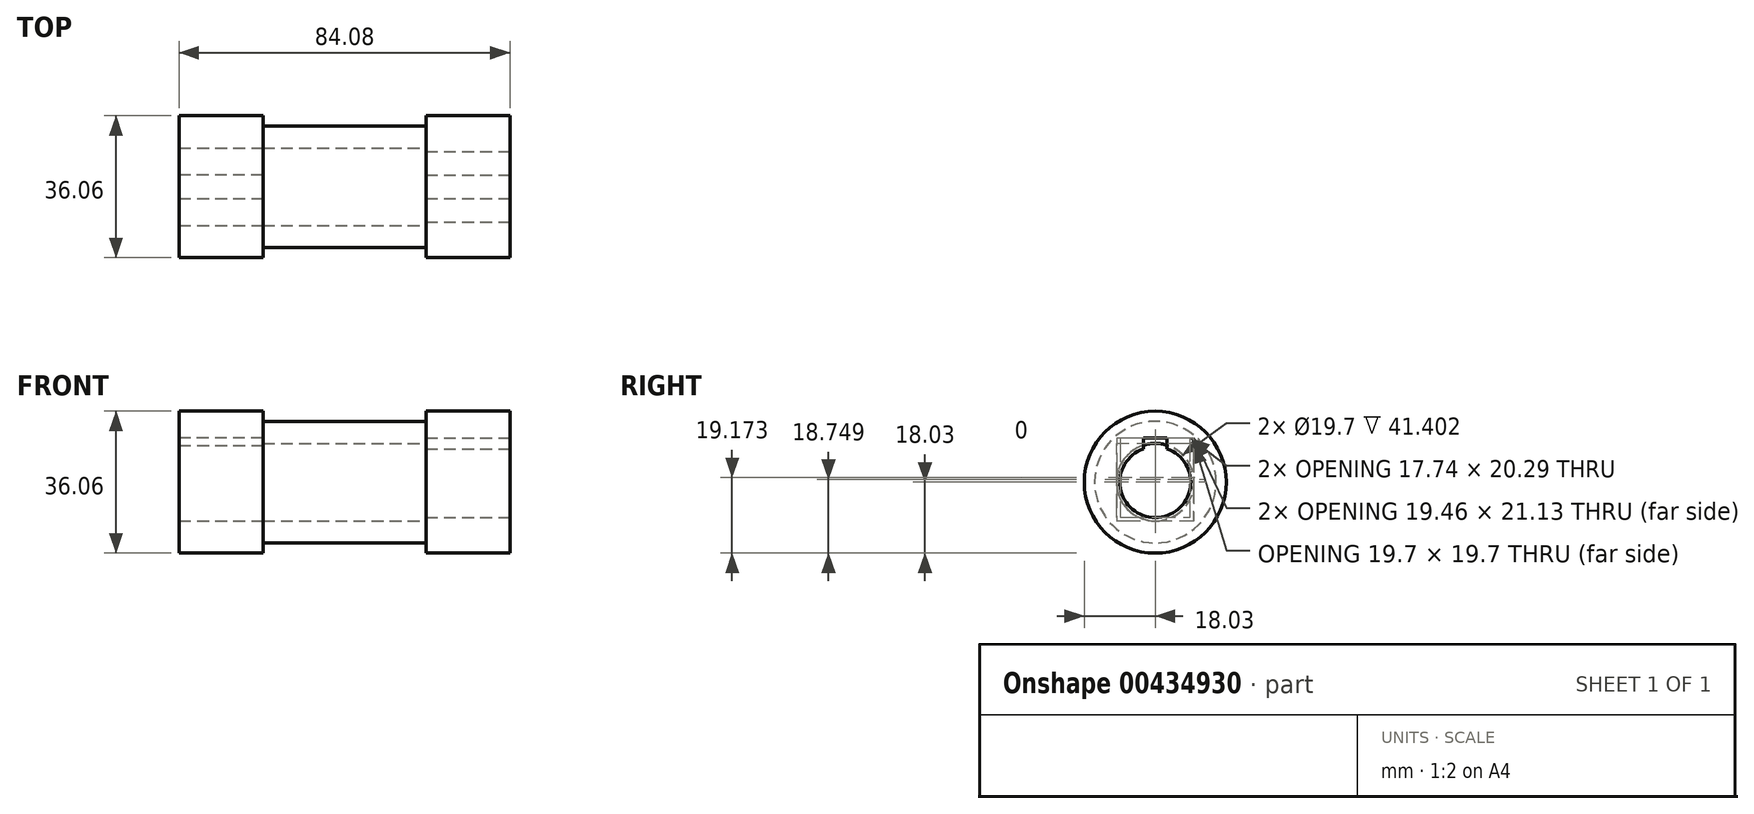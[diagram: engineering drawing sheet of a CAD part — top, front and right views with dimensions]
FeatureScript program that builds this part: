
annotation { "Feature Type Name" : "Feature", "Feature Type Description" : "" }
export const myFeature = defineFeature(function(context is Context, id is Id, definition is map)
    precondition{}
    {
        {
            var Q0;
            Q0=qCreatedBy(makeId("Right.planeOp"),FACE);
            cPlane(context, id + "F0", {"entities" : qUnion([Q0]), "cplaneType" : CPlaneType.OFFSET, "offset" : 42.04 * mm, "width" : 152.4 * mm, "height" : 152.4 * mm});
        }
        {
            var Q0;
            Q0=qCreatedBy(id+"F0.planeOp",FACE);
            var sketch = newSketch(context, id + "F1", { "sketchPlane" : qUnion([Q0])});
            skCircle(sketch, "E0", {"center": v(0, 0) * mm, "radius": 18.03 * mm});
            skArc(sketch, "E1", {"start": v(-3, 8.49) * mm, "mid": v(0, -9) * mm, "end": v(3, 8.49) * mm});
            skLineSegment(sketch, "E2", {"start": v(0, 0) * mm, "end": v(0, 9) * mm, "construction": true});
            skLineSegment(sketch, "E3.bottom", {"start": v(-3, 11.29) * mm, "end": v(3, 11.29) * mm});
            skLineSegment(sketch, "E3.left", {"start": v(-3, 11.29) * mm, "end": v(-3, 8.49) * mm});
            skLineSegment(sketch, "E3.right", {"start": v(3, 11.29) * mm, "end": v(3, 8.49) * mm});
            skPoint(sketch, "E3.middle", {"position": v(0, 9) * mm});
            skPoint(sketch, "E4", {"position": v(3, 8.49) * mm});
            skPoint(sketch, "E5.orphan", {"position": v(-3, 6.71) * mm});
            skPoint(sketch, "E6.orphan", {"position": v(3, 6.71) * mm});
            skSolve(sketch);
        }
        {
            var Q0;
            Q0 = qSketchRegion(id + "F1", true);
            extrude(context, id + "F2", {"entities" : qUnion([Q0]), "oppositeDirection" : true, "depth" : 21.34 * mm});
        }
        {
            var Q0;
            Q0=makeQuery(id+"F2.opExtrude","SWEPT_BODY",BODY,{"disambiguationData":[OSD([sQuery(id+"F1.wireOp",EDGE,"E0"),sQuery(id+"F1.wireOp",EDGE,"E1"),sQuery(id+"F1.wireOp",EDGE,"E3.bottom"),sQuery(id+"F1.wireOp",EDGE,"E3.left"),sQuery(id+"F1.wireOp",EDGE,"E3.right")])]});
            var Q1;
            Q1=qCreatedBy(makeId("Right.planeOp"),FACE);
            mirror(context, id + "F3", {"entities" : qUnion([Q0]), "mirrorPlane" : qUnion([Q1])});
        }
        {
            var Q0;
            Q0=makeQuery(id+"F2.opExtrude","CAP_FACE",FACE,{"disambiguationData":[OSD([sQuery(id+"F1.wireOp",EDGE,"E0"),sQuery(id+"F1.wireOp",EDGE,"E1"),sQuery(id+"F1.wireOp",EDGE,"E3.bottom"),sQuery(id+"F1.wireOp",EDGE,"E3.left"),sQuery(id+"F1.wireOp",EDGE,"E3.right")])],"isStart":false});
            var sketch = newSketch(context, id + "F4", { "sketchPlane" : qUnion([Q0])});
            skCircle(sketch, "E7", {"center": v(0, 0) * mm, "radius": 15.44 * mm});
            skSolve(sketch);
        }
        {
            var Q0;
            Q0 = qSketchRegion(id + "F4", true);
            var Q1;
            Q1=makeQuery(id+"F3.opPattern","COPY",FACE,{"derivedFrom":makeQuery(id+"F2.opExtrude","CAP_FACE",FACE,{"disambiguationData":[OSD([sQuery(id+"F1.wireOp",EDGE,"E0"),sQuery(id+"F1.wireOp",EDGE,"E1"),sQuery(id+"F1.wireOp",EDGE,"E3.bottom"),sQuery(id+"F1.wireOp",EDGE,"E3.left"),sQuery(id+"F1.wireOp",EDGE,"E3.right")])],"isStart":false}),"instanceName":"1"});
            extrude(context, id + "F5", {"entities" : qUnion([Q0]), "endBound" : BoundingType.UP_TO_SURFACE, "endBoundEntityFace" : qUnion([Q1]), "depth" : 25.4 * mm});
        }
        {
            var Q0;
            Q0=makeQuery(id+"F5.opExtrude","CAP_FACE",FACE,{"disambiguationData":[OSD([sQuery(id+"F4.wireOp",EDGE,"E7")])],"isStart":true});
            var sketch = newSketch(context, id + "F6", { "sketchPlane" : qUnion([Q0])});
            skCircle(sketch, "E8", {"center": v(0, 0) * mm, "radius": 9.85 * mm});
            skSolve(sketch);
        }
        {
            var Q0;
            Q0 = qSketchRegion(id + "F6", true);
            extrude(context, id + "F7", {"entities" : qUnion([Q0]), "operationType" : NewBodyOperationType.REMOVE, "endBound" : BoundingType.THROUGH_ALL, "oppositeDirection" : true, "depth" : 25.4 * mm});
        }
    });
